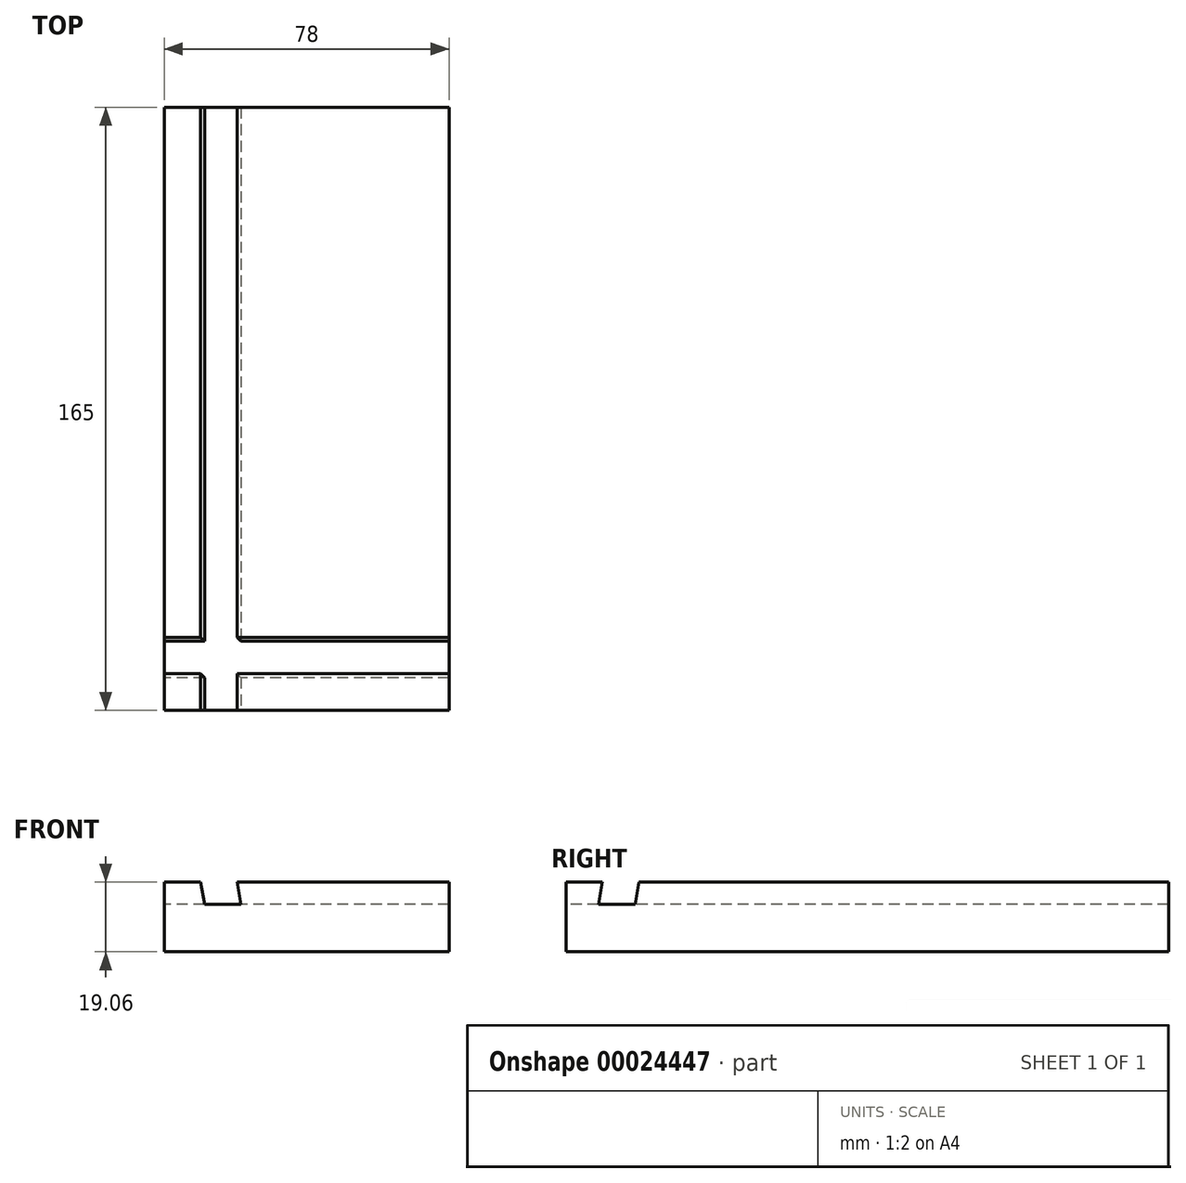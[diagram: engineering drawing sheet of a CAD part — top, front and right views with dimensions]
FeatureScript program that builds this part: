
annotation { "Feature Type Name" : "Feature", "Feature Type Description" : "" }
export const myFeature = defineFeature(function(context is Context, id is Id, definition is map)
    precondition{}
    {
        {
            var Q0;
            Q0=qCreatedBy(makeId("Front.planeOp"),FACE);
            var sketch = newSketch(context, id + "F0", { "sketchPlane" : qUnion([Q0])});
            skLineSegment(sketch, "E0.bottom", {"start": v(-39, 9.52) * mm, "end": v(39, 9.52) * mm});
            skLineSegment(sketch, "E0.top", {"start": v(-39, -9.52) * mm, "end": v(39, -9.52) * mm});
            skLineSegment(sketch, "E0.left", {"start": v(-39, 9.52) * mm, "end": v(-39, -9.52) * mm});
            skLineSegment(sketch, "E0.right", {"start": v(39, 9.52) * mm, "end": v(39, -9.52) * mm});
            skLineSegment(sketch, "E1", {"start": v(39, 9.52) * mm, "end": v(-39, -9.52) * mm, "construction": true});
            skSolve(sketch);
        }
        {
            var Q0;
            Q0=makeQuery(id+"F0.imprint","IMPRINT",FACE,{"disambiguationData":[TD([[makeQuery(id+"F0.imprint","IMPRINT",EDGE,{"derivedFrom":sQuery(id+"F0.wireOp",EDGE,"E0.bottom")}),-1.0]])]});
            extrude(context, id + "F1", {"entities" : qUnion([Q0]), "endBound" : BoundingType.SYMMETRIC, "depth" : 165 * mm});
        }
        {
            var Q0;
            Q0=qCreatedBy(makeId("Front.planeOp"),FACE);
            var sketch = newSketch(context, id + "F2", { "sketchPlane" : qUnion([Q0])});
            skLineSegment(sketch, "E2", {"start": v(-29, 9.52) * mm, "end": v(-27.94, 3.52) * mm});
            skLineSegment(sketch, "E3", {"start": v(-27.94, 3.52) * mm, "end": v(-17.94, 3.52) * mm});
            skLineSegment(sketch, "E4", {"start": v(-17.94, 3.52) * mm, "end": v(-19, 9.52) * mm});
            skLineSegment(sketch, "E5", {"start": v(-29, 9.52) * mm, "end": v(-19, 9.52) * mm});
            skSolve(sketch);
        }
        {
            var Q0;
            Q0 = qSketchRegion(id + "F2", true);
            extrude(context, id + "F3", {"entities" : qUnion([Q0]), "operationType" : NewBodyOperationType.REMOVE, "endBound" : BoundingType.SYMMETRIC, "oppositeDirection" : true, "depth" : 170 * mm});
        }
        {
            var Q0;
            Q0=qCreatedBy(makeId("Right.planeOp"),FACE);
            var sketch = newSketch(context, id + "F4", { "sketchPlane" : qUnion([Q0])});
            skLineSegment(sketch, "E6", {"start": v(-72.5, 9.52) * mm, "end": v(-73.56, 3.52) * mm});
            skLineSegment(sketch, "E7", {"start": v(-73.56, 3.52) * mm, "end": v(-63.56, 3.52) * mm});
            skLineSegment(sketch, "E8", {"start": v(-63.56, 3.52) * mm, "end": v(-62.5, 9.52) * mm});
            skLineSegment(sketch, "E9", {"start": v(-72.5, 9.52) * mm, "end": v(-62.5, 9.52) * mm});
            skSolve(sketch);
        }
        {
            var Q0;
            Q0 = qSketchRegion(id + "F4", true);
            extrude(context, id + "F5", {"entities" : qUnion([Q0]), "operationType" : NewBodyOperationType.REMOVE, "endBound" : BoundingType.SYMMETRIC, "depth" : 85 * mm});
        }
    });
